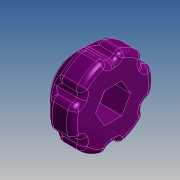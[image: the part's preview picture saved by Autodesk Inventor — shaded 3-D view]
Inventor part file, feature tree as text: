
AUTODESK INVENTOR PART (.ipt)
format: ipt  version: 2015 SP1 (Build 190203100, 203)  size: 539,136 bytes
history: native  units: mm
features: sketch x3, extrude x2, fillet x2, revolve x1, mirror x1, pattern_circular x1
ambient origin geometry x8: Origin, YZ Plane, XZ Plane, XY Plane, X Axis, Y Axis, Z Axis, Center Point
bodies: Solid1 (feature_tree)
feature tree (10):
  revolve  "Revolution1"  Angle=45.0deg
  extrude  "Extrusion1"  Depth=4.0mm
  extrude  "Extrusion2"  TaperAngle=90.0deg  [1 undecoded]
  fillet  "Fillet1"  Radius=5.5mm
  mirror  "Mirror1"
  pattern_circular  "Circular Pattern1"  [2 undecoded]
  fillet  "Fillet2"  Radius=1.308997mm
  sketch  "Sketch1"  dims[d0=3.3mm d1=45.0deg]
  sketch  "Sketch2"  dims[d2=15.0mm d3=4.0mm]
  sketch  "Sketch3"  dims[d4=7.0mm d5=90.0deg d6=5.5mm d7=4.0mm d8=0.0mm d9=1.308997mm d10=1.0mm d11=4.0mm d12=0.0mm d13=1.0mm d14=60.0mm d15=360.0deg d17=1.0mm]
note: 3 required parameter values undecoded (feature->parameter linkage not recoverable at this tier; creation-order binding heuristic only, values carry confidence <= 0.55)
